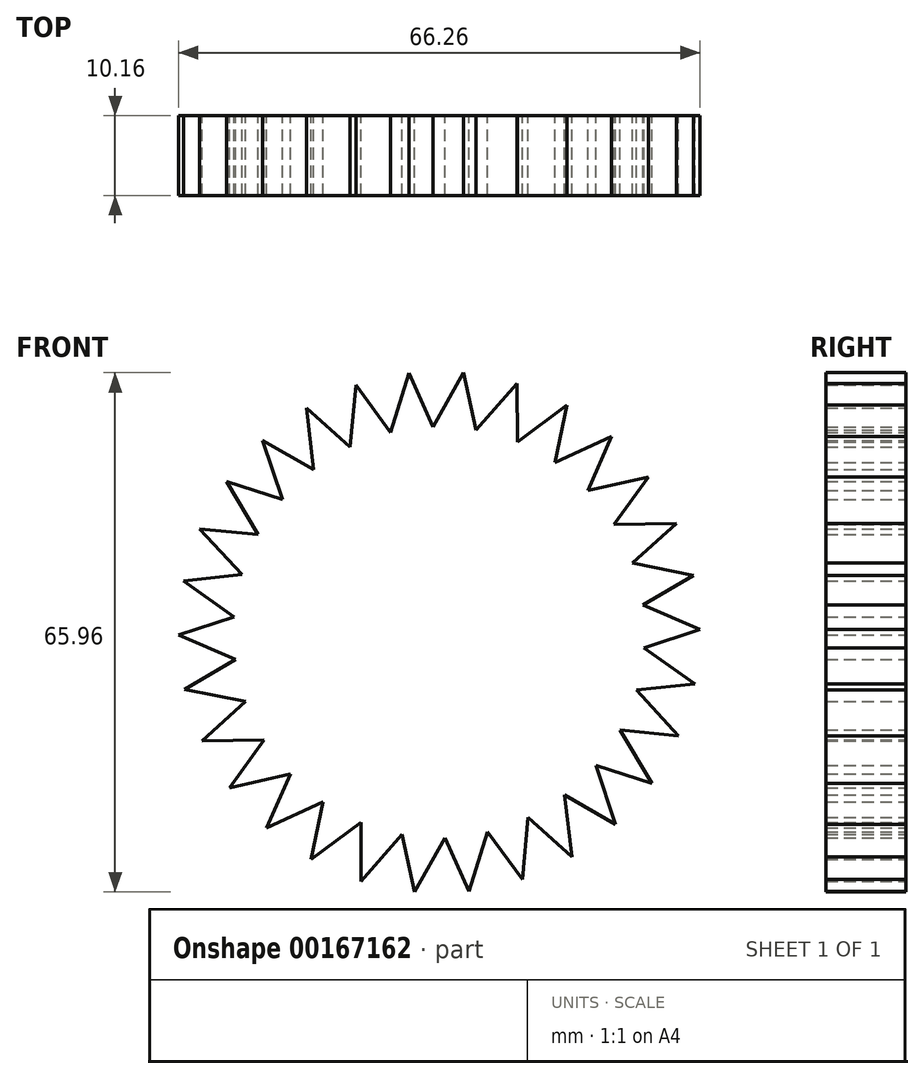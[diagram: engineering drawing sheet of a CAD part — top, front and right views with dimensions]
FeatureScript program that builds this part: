
annotation { "Feature Type Name" : "Feature", "Feature Type Description" : "" }
export const myFeature = defineFeature(function(context is Context, id is Id, definition is map)
    precondition{}
    {
        {
            var Q0;
            Q0=qCreatedBy(makeId("Front.planeOp"),FACE);
            var sketch = newSketch(context, id + "F0", { "sketchPlane" : qUnion([Q0])});
            skCircle(sketch, "E0", {"center": v(0, 0) * mm, "radius": 25.4 * mm});
            skLineSegment(sketch, "E1", {"start": v(-19.63, 16.12) * mm, "end": v(-22.43, 24.38) * mm});
            skLineSegment(sketch, "E2", {"start": v(-22.43, 24.38) * mm, "end": v(-15.28, 20.29) * mm});
            skLineSegment(sketch, "E3.1.0", {"start": v(-27, 19.19) * mm, "end": v(-19.17, 16.67) * mm});
            skLineSegment(sketch, "E3.1.1", {"start": v(-22.55, 11.68) * mm, "end": v(-27, 19.19) * mm});
            skLineSegment(sketch, "E3.2.0", {"start": v(-30.4, 13.16) * mm, "end": v(-22.21, 12.32) * mm});
            skLineSegment(sketch, "E3.2.1", {"start": v(-24.49, 6.74) * mm, "end": v(-30.4, 13.16) * mm});
            skLineSegment(sketch, "E3.3.0", {"start": v(-32.48, 6.55) * mm, "end": v(-24.29, 7.43) * mm});
            skLineSegment(sketch, "E3.3.1", {"start": v(-25.36, 1.5) * mm, "end": v(-32.48, 6.55) * mm});
            skLineSegment(sketch, "E3.4.0", {"start": v(-33.13, -0.35) * mm, "end": v(-25.3, 2.22) * mm});
            skLineSegment(sketch, "E3.4.1", {"start": v(-25.11, -3.8) * mm, "end": v(-33.13, -0.35) * mm});
            skLineSegment(sketch, "E3.5.0", {"start": v(-32.33, -7.23) * mm, "end": v(-25.21, -3.1) * mm});
            skLineSegment(sketch, "E3.5.1", {"start": v(-23.77, -8.94) * mm, "end": v(-32.33, -7.23) * mm});
            skLineSegment(sketch, "E3.6.0", {"start": v(-30.12, -13.8) * mm, "end": v(-24.02, -8.27) * mm});
            skLineSegment(sketch, "E3.6.1", {"start": v(-21.4, -13.69) * mm, "end": v(-30.12, -13.8) * mm});
            skLineSegment(sketch, "E3.7.0", {"start": v(-26.6, -19.75) * mm, "end": v(-21.77, -13.08) * mm});
            skLineSegment(sketch, "E3.7.1", {"start": v(-18.08, -17.84) * mm, "end": v(-26.6, -19.75) * mm});
            skLineSegment(sketch, "E3.8.0", {"start": v(-21.9, -24.85) * mm, "end": v(-18.58, -17.32) * mm});
            skLineSegment(sketch, "E3.8.1", {"start": v(-13.98, -21.2) * mm, "end": v(-21.9, -24.85) * mm});
            skLineSegment(sketch, "E3.9.0", {"start": v(-16.26, -28.86) * mm, "end": v(-14.57, -20.8) * mm});
            skLineSegment(sketch, "E3.9.1", {"start": v(-9.26, -23.65) * mm, "end": v(-16.26, -28.86) * mm});
            skLineSegment(sketch, "E3.10.0", {"start": v(-9.9, -31.61) * mm, "end": v(-9.93, -23.38) * mm});
            skLineSegment(sketch, "E3.10.1", {"start": v(-4.14, -25.06) * mm, "end": v(-9.9, -31.61) * mm});
            skLineSegment(sketch, "E3.11.0", {"start": v(-3.12, -32.98) * mm, "end": v(-4.85, -24.93) * mm});
            skLineSegment(sketch, "E3.11.1", {"start": v(1.16, -25.37) * mm, "end": v(-3.12, -32.98) * mm});
            skLineSegment(sketch, "E3.12.0", {"start": v(3.81, -32.9) * mm, "end": v(0.44, -25.4) * mm});
            skLineSegment(sketch, "E3.12.1", {"start": v(6.4, -24.58) * mm, "end": v(3.81, -32.9) * mm});
            skLineSegment(sketch, "E3.13.0", {"start": v(10.57, -31.4) * mm, "end": v(5.7, -24.75) * mm});
            skLineSegment(sketch, "E3.13.1", {"start": v(11.38, -22.7) * mm, "end": v(10.57, -31.4) * mm});
            skLineSegment(sketch, "E3.14.0", {"start": v(16.87, -28.51) * mm, "end": v(10.73, -23.02) * mm});
            skLineSegment(sketch, "E3.14.1", {"start": v(15.85, -19.85) * mm, "end": v(16.87, -28.51) * mm});
            skLineSegment(sketch, "E3.15.0", {"start": v(22.43, -24.38) * mm, "end": v(15.28, -20.29) * mm});
            skLineSegment(sketch, "E3.15.1", {"start": v(19.63, -16.12) * mm, "end": v(22.43, -24.38) * mm});
            skLineSegment(sketch, "E3.16.0", {"start": v(27, -19.19) * mm, "end": v(19.17, -16.67) * mm});
            skLineSegment(sketch, "E3.16.1", {"start": v(22.55, -11.68) * mm, "end": v(27, -19.19) * mm});
            skLineSegment(sketch, "E3.17.0", {"start": v(30.4, -13.16) * mm, "end": v(22.21, -12.32) * mm});
            skLineSegment(sketch, "E3.17.1", {"start": v(24.49, -6.74) * mm, "end": v(30.4, -13.16) * mm});
            skLineSegment(sketch, "E3.18.0", {"start": v(32.48, -6.55) * mm, "end": v(24.29, -7.43) * mm});
            skLineSegment(sketch, "E3.18.1", {"start": v(25.36, -1.5) * mm, "end": v(32.48, -6.55) * mm});
            skLineSegment(sketch, "E3.19.0", {"start": v(33.13, 0.35) * mm, "end": v(25.3, -2.22) * mm});
            skLineSegment(sketch, "E3.19.1", {"start": v(25.11, 3.8) * mm, "end": v(33.13, 0.35) * mm});
            skLineSegment(sketch, "E3.20.0", {"start": v(32.33, 7.23) * mm, "end": v(25.21, 3.1) * mm});
            skLineSegment(sketch, "E3.20.1", {"start": v(23.77, 8.94) * mm, "end": v(32.33, 7.23) * mm});
            skLineSegment(sketch, "E3.21.0", {"start": v(30.12, 13.8) * mm, "end": v(24.02, 8.27) * mm});
            skLineSegment(sketch, "E3.21.1", {"start": v(21.4, 13.69) * mm, "end": v(30.12, 13.8) * mm});
            skLineSegment(sketch, "E3.22.0", {"start": v(26.6, 19.75) * mm, "end": v(21.77, 13.08) * mm});
            skLineSegment(sketch, "E3.22.1", {"start": v(18.08, 17.84) * mm, "end": v(26.6, 19.75) * mm});
            skLineSegment(sketch, "E3.23.0", {"start": v(21.9, 24.85) * mm, "end": v(18.58, 17.32) * mm});
            skLineSegment(sketch, "E3.23.1", {"start": v(13.98, 21.2) * mm, "end": v(21.9, 24.85) * mm});
            skLineSegment(sketch, "E3.24.0", {"start": v(16.26, 28.86) * mm, "end": v(14.57, 20.8) * mm});
            skLineSegment(sketch, "E3.24.1", {"start": v(9.26, 23.65) * mm, "end": v(16.26, 28.86) * mm});
            skLineSegment(sketch, "E3.25.0", {"start": v(9.9, 31.61) * mm, "end": v(9.93, 23.38) * mm});
            skLineSegment(sketch, "E3.25.1", {"start": v(4.14, 25.06) * mm, "end": v(9.9, 31.61) * mm});
            skLineSegment(sketch, "E3.26.0", {"start": v(3.12, 32.98) * mm, "end": v(4.85, 24.93) * mm});
            skLineSegment(sketch, "E3.26.1", {"start": v(-1.16, 25.37) * mm, "end": v(3.12, 32.98) * mm});
            skLineSegment(sketch, "E3.27.0", {"start": v(-3.81, 32.9) * mm, "end": v(-0.44, 25.4) * mm});
            skLineSegment(sketch, "E3.27.1", {"start": v(-6.4, 24.58) * mm, "end": v(-3.81, 32.9) * mm});
            skLineSegment(sketch, "E3.28.0", {"start": v(-10.57, 31.4) * mm, "end": v(-5.7, 24.75) * mm});
            skLineSegment(sketch, "E3.28.1", {"start": v(-11.38, 22.7) * mm, "end": v(-10.57, 31.4) * mm});
            skLineSegment(sketch, "E3.29.0", {"start": v(-16.87, 28.51) * mm, "end": v(-10.73, 23.02) * mm});
            skLineSegment(sketch, "E3.29.1", {"start": v(-15.85, 19.85) * mm, "end": v(-16.87, 28.51) * mm});
            skSolve(sketch);
        }
        {
            var Q0;
            Q0 = qSketchRegion(id + "F0", true);
            extrude(context, id + "F1", {"entities" : qUnion([Q0]), "depth" : 10.16 * mm});
        }
        {
            var Q0;
            Q0=qCreatedBy(makeId("Front.planeOp"),FACE);
            var sketch = newSketch(context, id + "F2", { "sketchPlane" : qUnion([Q0])});
            skCircle(sketch, "E4", {"center": v(0, 0) * mm, "radius": 25.4 * mm});
            skSolve(sketch);
        }
        {
            var Q0;
            Q0 = qSketchRegion(id + "F2", true);
            extrude(context, id + "F3", {"entities" : qUnion([Q0]), "operationType" : NewBodyOperationType.ADD, "depth" : 10.16 * mm});
        }
    });
